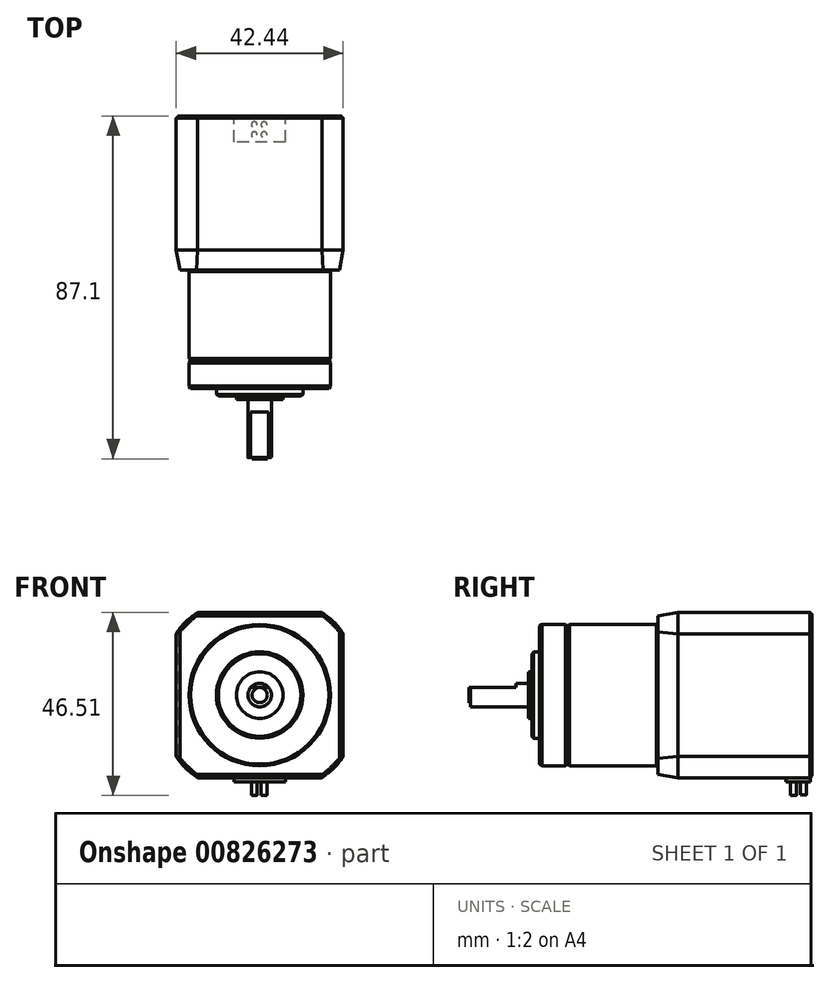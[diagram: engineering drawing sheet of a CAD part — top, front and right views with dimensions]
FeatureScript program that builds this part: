
annotation { "Feature Type Name" : "Feature", "Feature Type Description" : "" }
export const myFeature = defineFeature(function(context is Context, id is Id, definition is map)
    precondition{}
    {
        {
            var Q0;
            Q0=qCreatedBy(makeId("Front.planeOp"),FACE);
            var sketch = newSketch(context, id + "F0", { "sketchPlane" : qUnion([Q0])});
            skLineSegment(sketch, "E0", {"start": v(-21.22, -15.53) * mm, "end": v(-21.22, 15.53) * mm});
            skLineSegment(sketch, "E1", {"start": v(-6.73, -22.34) * mm, "end": v(6.27, -22.34) * mm});
            skFitSpline(sketch, "E2", {"points": [v(-21.22, 15.53) * mm, v(-15.77, 21) * mm], "startDerivative": vector(4.94, 6.8) * mm, "endDerivative": vector(6.38, 4.96) * mm});
            skFitSpline(sketch, "E3", {"points": [v(-20.22, 16.05) * mm, v(-16.08, 20.16) * mm], "startDerivative": vector(4, 4.56) * mm, "endDerivative": vector(4.18, 3.78) * mm});
            skLineSegment(sketch, "E4", {"start": v(-16.83, 20.16) * mm, "end": v(-16.08, 20.16) * mm});
            skLineSegment(sketch, "E5", {"start": v(-20.22, 16.82) * mm, "end": v(-20.22, 16.05) * mm});
            skCircle(sketch, "E6", {"center": v(-15.75, 15.5) * mm, "radius": 2.2 * mm});
            skCircle(sketch, "E7", {"center": v(-15.75, 15.5) * mm, "radius": 2.5 * mm});
            skLineSegment(sketch, "E8", {"start": v(-16.76, 15.5) * mm, "end": v(-16.76, 16.1) * mm});
            skLineSegment(sketch, "E9", {"start": v(-16.76, 16.1) * mm, "end": v(-16.35, 16.53) * mm});
            skLineSegment(sketch, "E10", {"start": v(-16.35, 16.53) * mm, "end": v(-15.75, 16.53) * mm});
            skLineSegment(sketch, "E11", {"start": v(-15.75, 15.5) * mm, "end": v(-15.75, 16.53) * mm});
            skLineSegment(sketch, "E12", {"start": v(-15.75, 15.5) * mm, "end": v(-16.76, 15.5) * mm});
            skLineSegment(sketch, "E13", {"start": v(-15.75, 15.5) * mm, "end": v(-15.78, 18.62) * mm, "construction": true});
            skLineSegment(sketch, "E14", {"start": v(-15.75, 15.5) * mm, "end": v(-15.73, 12.29) * mm, "construction": true});
            skLineSegment(sketch, "E15", {"start": v(-15.73, 12.29) * mm, "end": v(-15.75, 15.5) * mm, "construction": true});
            skLineSegment(sketch, "E16", {"start": v(-15.75, 15.5) * mm, "end": v(-12.33, 15.53) * mm, "construction": true});
            skLineSegment(sketch, "E17", {"start": v(-15.75, 15.5) * mm, "end": v(-18.75, 15.48) * mm, "construction": true});
            skLineSegment(sketch, "E18.MirrorCS", {"start": v(-15.17, 16.54) * mm, "end": v(-15.77, 16.53) * mm});
            skLineSegment(sketch, "E19.MirrorCS", {"start": v(-14.75, 16.1) * mm, "end": v(-15.17, 16.54) * mm});
            skLineSegment(sketch, "E20.MirrorCS", {"start": v(-14.75, 15.5) * mm, "end": v(-14.75, 16.1) * mm});
            skLineSegment(sketch, "E21.MirrorCS", {"start": v(-14.75, 15.5) * mm, "end": v(-14.75, 14.9) * mm});
            skLineSegment(sketch, "E22.MirrorCS", {"start": v(-14.75, 14.9) * mm, "end": v(-15.15, 14.47) * mm});
            skLineSegment(sketch, "E23.MirrorCS", {"start": v(-15.15, 14.47) * mm, "end": v(-15.75, 14.47) * mm});
            skLineSegment(sketch, "E24.MirrorCS", {"start": v(-16.34, 14.46) * mm, "end": v(-15.74, 14.47) * mm});
            skLineSegment(sketch, "E25.MirrorCS", {"start": v(-16.75, 14.9) * mm, "end": v(-16.34, 14.46) * mm});
            skLineSegment(sketch, "E26.MirrorCS", {"start": v(-16.76, 15.5) * mm, "end": v(-16.75, 14.9) * mm});
            skLineSegment(sketch, "E27", {"start": v(0, 0) * mm, "end": v(-21.22, 0) * mm, "construction": true});
            skLineSegment(sketch, "E28", {"start": v(0, 0) * mm, "end": v(0, 21) * mm, "construction": true});
            skCircle(sketch, "E29.MirrorC", {"center": v(15.75, 15.5) * mm, "radius": 2.2 * mm});
            skCircle(sketch, "E30.MirrorC", {"center": v(15.75, 15.5) * mm, "radius": 2.5 * mm});
            skLineSegment(sketch, "E31.MirrorCS", {"start": v(14.75, 15.5) * mm, "end": v(14.75, 14.9) * mm});
            skLineSegment(sketch, "E32.MirrorCS", {"start": v(14.75, 15.5) * mm, "end": v(14.75, 16.1) * mm});
            skLineSegment(sketch, "E33.MirrorCS", {"start": v(14.75, 16.1) * mm, "end": v(15.17, 16.54) * mm});
            skLineSegment(sketch, "E34.MirrorCS", {"start": v(15.17, 16.54) * mm, "end": v(15.77, 16.53) * mm});
            skLineSegment(sketch, "E35.MirrorCS", {"start": v(16.35, 16.53) * mm, "end": v(15.75, 16.53) * mm});
            skLineSegment(sketch, "E36.MirrorCS", {"start": v(16.76, 16.1) * mm, "end": v(16.35, 16.53) * mm});
            skLineSegment(sketch, "E37.MirrorCS", {"start": v(16.76, 15.5) * mm, "end": v(16.76, 16.1) * mm});
            skLineSegment(sketch, "E38.MirrorCS", {"start": v(16.76, 15.5) * mm, "end": v(16.75, 14.9) * mm});
            skLineSegment(sketch, "E39.MirrorCS", {"start": v(16.75, 14.9) * mm, "end": v(16.34, 14.46) * mm});
            skLineSegment(sketch, "E40.MirrorCS", {"start": v(16.34, 14.46) * mm, "end": v(15.74, 14.47) * mm});
            skLineSegment(sketch, "E41.MirrorCS", {"start": v(15.75, 15.5) * mm, "end": v(18.75, 15.48) * mm, "construction": true});
            skLineSegment(sketch, "E42.MirrorCS", {"start": v(15.75, 15.5) * mm, "end": v(12.33, 15.53) * mm, "construction": true});
            skLineSegment(sketch, "E43.MirrorCS", {"start": v(15.75, 15.5) * mm, "end": v(15.78, 18.62) * mm, "construction": true});
            skLineSegment(sketch, "E44.MirrorCS", {"start": v(15.75, 15.5) * mm, "end": v(15.73, 12.29) * mm, "construction": true});
            skFitSpline(sketch, "E45.MirrorCS", {"points": [v(21.22, 15.53) * mm, v(15.77, 21) * mm], "startDerivative": vector(-4.94, 6.8) * mm, "endDerivative": vector(-6.38, 4.96) * mm});
            skFitSpline(sketch, "E46.MirrorCS", {"points": [v(20.22, 16.05) * mm, v(16.08, 20.16) * mm], "startDerivative": vector(-4, 4.56) * mm, "endDerivative": vector(-4.18, 3.78) * mm});
            skLineSegment(sketch, "E47.MirrorCS", {"start": v(16.83, 20.16) * mm, "end": v(16.08, 20.16) * mm});
            skLineSegment(sketch, "E48", {"start": v(-15.77, 21) * mm, "end": v(0, 21) * mm});
            skLineSegment(sketch, "E49.MirrorCS", {"start": v(15.77, 21) * mm, "end": v(0, 21) * mm});
            skLineSegment(sketch, "E50.MirrorCS", {"start": v(20.22, 16.82) * mm, "end": v(20.22, 16.05) * mm});
            skLineSegment(sketch, "E51.MirrorCS", {"start": v(21.22, -15.53) * mm, "end": v(21.22, 15.53) * mm});
            skLineSegment(sketch, "E52.MirrorCS", {"start": v(-15.77, -21) * mm, "end": v(0, -21) * mm});
            skLineSegment(sketch, "E53.MirrorCS", {"start": v(-16.83, -20.16) * mm, "end": v(-16.08, -20.16) * mm});
            skFitSpline(sketch, "E54.MirrorCS", {"points": [v(-20.22, -16.05) * mm, v(-16.08, -20.16) * mm], "startDerivative": vector(4, -4.56) * mm, "endDerivative": vector(4.18, -3.78) * mm});
            skFitSpline(sketch, "E55.MirrorCS", {"points": [v(-21.22, -15.53) * mm, v(-15.77, -21) * mm], "startDerivative": vector(4.94, -6.8) * mm, "endDerivative": vector(6.38, -4.96) * mm});
            skLineSegment(sketch, "E56.MirrorCS", {"start": v(-20.22, -16.82) * mm, "end": v(-20.22, -16.05) * mm});
            skLineSegment(sketch, "E57.MirrorCS", {"start": v(-21.22, 15.53) * mm, "end": v(-21.22, -15.53) * mm});
            skCircle(sketch, "E58.MirrorC", {"center": v(-15.75, -15.5) * mm, "radius": 2.5 * mm});
            skCircle(sketch, "E59.MirrorC", {"center": v(-15.75, -15.5) * mm, "radius": 2.2 * mm});
            skLineSegment(sketch, "E60.MirrorCS", {"start": v(-16.75, -14.9) * mm, "end": v(-16.34, -14.46) * mm});
            skLineSegment(sketch, "E61.MirrorCS", {"start": v(-16.34, -14.46) * mm, "end": v(-15.74, -14.47) * mm});
            skLineSegment(sketch, "E62.MirrorCS", {"start": v(-15.15, -14.47) * mm, "end": v(-15.75, -14.47) * mm});
            skLineSegment(sketch, "E63.MirrorCS", {"start": v(-15.17, -16.54) * mm, "end": v(-15.77, -16.53) * mm});
            skLineSegment(sketch, "E64.MirrorCS", {"start": v(-14.75, -16.1) * mm, "end": v(-15.17, -16.54) * mm});
            skLineSegment(sketch, "E65.MirrorCS", {"start": v(-14.75, -15.5) * mm, "end": v(-14.75, -16.1) * mm});
            skLineSegment(sketch, "E66.MirrorCS", {"start": v(-14.75, -15.5) * mm, "end": v(-14.75, -14.9) * mm});
            skLineSegment(sketch, "E67.MirrorCS", {"start": v(-14.75, -14.9) * mm, "end": v(-15.15, -14.47) * mm});
            skLineSegment(sketch, "E68.MirrorCS", {"start": v(-16.76, -15.5) * mm, "end": v(-16.75, -14.9) * mm});
            skLineSegment(sketch, "E69.MirrorCS", {"start": v(-16.76, -16.1) * mm, "end": v(-16.35, -16.53) * mm});
            skLineSegment(sketch, "E70.MirrorCS", {"start": v(-16.76, -15.5) * mm, "end": v(-16.76, -16.1) * mm});
            skLineSegment(sketch, "E71.MirrorCS", {"start": v(-16.35, -16.53) * mm, "end": v(-15.75, -16.53) * mm});
            skLineSegment(sketch, "E72.MirrorCS", {"start": v(14.75, 14.9) * mm, "end": v(15.15, 14.47) * mm});
            skLineSegment(sketch, "E73.MirrorCS", {"start": v(15.15, 14.47) * mm, "end": v(15.75, 14.47) * mm});
            skLineSegment(sketch, "E74.MirrorCS", {"start": v(16.83, -20.16) * mm, "end": v(16.08, -20.16) * mm});
            skLineSegment(sketch, "E75.MirrorCS", {"start": v(15.77, -21) * mm, "end": v(0, -21) * mm});
            skFitSpline(sketch, "E76.MirrorCS", {"points": [v(21.22, -15.53) * mm, v(15.77, -21) * mm], "startDerivative": vector(-4.94, -6.8) * mm, "endDerivative": vector(-6.38, -4.96) * mm});
            skFitSpline(sketch, "E77.MirrorCS", {"points": [v(20.22, -16.05) * mm, v(16.08, -20.16) * mm], "startDerivative": vector(-4, -4.56) * mm, "endDerivative": vector(-4.18, -3.78) * mm});
            skLineSegment(sketch, "E78.MirrorCS", {"start": v(20.22, -16.82) * mm, "end": v(20.22, -16.05) * mm});
            skCircle(sketch, "E79.MirrorC", {"center": v(15.75, -15.5) * mm, "radius": 2.2 * mm});
            skCircle(sketch, "E80.MirrorC", {"center": v(15.75, -15.5) * mm, "radius": 2.5 * mm});
            skLineSegment(sketch, "E81.MirrorCS", {"start": v(16.75, -14.9) * mm, "end": v(16.34, -14.46) * mm});
            skLineSegment(sketch, "E82.MirrorCS", {"start": v(16.34, -14.46) * mm, "end": v(15.74, -14.47) * mm});
            skLineSegment(sketch, "E83.MirrorCS", {"start": v(15.15, -14.47) * mm, "end": v(15.75, -14.47) * mm});
            skLineSegment(sketch, "E84.MirrorCS", {"start": v(14.75, -14.9) * mm, "end": v(15.15, -14.47) * mm});
            skLineSegment(sketch, "E85.MirrorCS", {"start": v(14.75, -15.5) * mm, "end": v(14.75, -14.9) * mm});
            skLineSegment(sketch, "E86.MirrorCS", {"start": v(14.75, -15.5) * mm, "end": v(14.75, -16.1) * mm});
            skLineSegment(sketch, "E87.MirrorCS", {"start": v(14.75, -16.1) * mm, "end": v(15.17, -16.54) * mm});
            skLineSegment(sketch, "E88.MirrorCS", {"start": v(15.17, -16.54) * mm, "end": v(15.77, -16.53) * mm});
            skLineSegment(sketch, "E89.MirrorCS", {"start": v(16.35, -16.53) * mm, "end": v(15.75, -16.53) * mm});
            skLineSegment(sketch, "E90.MirrorCS", {"start": v(16.76, -16.1) * mm, "end": v(16.35, -16.53) * mm});
            skLineSegment(sketch, "E91.MirrorCS", {"start": v(16.76, -15.5) * mm, "end": v(16.76, -16.1) * mm});
            skLineSegment(sketch, "E92.MirrorCS", {"start": v(16.76, -15.5) * mm, "end": v(16.75, -14.9) * mm});
            skLineSegment(sketch, "E93", {"start": v(-16.08, 20.16) * mm, "end": v(0, 20.16) * mm});
            skFitSpline(sketch, "E94", {"points": [v(21.22, 15.53) * mm, v(15.77, 21) * mm], "startDerivative": vector(-4.94, 6.8) * mm, "endDerivative": vector(-6.38, 4.96) * mm});
            skLineSegment(sketch, "E95", {"start": v(16.08, 20.16) * mm, "end": v(16.08, 20.16) * mm});
            skLineSegment(sketch, "E96", {"start": v(16.08, 20.16) * mm, "end": v(0, 20.16) * mm});
            skLineSegment(sketch, "E97", {"start": v(16.08, -20.16) * mm, "end": v(0, -20.16) * mm});
            skFitSpline(sketch, "E98", {"points": [v(21.22, -15.53) * mm, v(15.77, -21) * mm], "startDerivative": vector(-4.94, -6.8) * mm, "endDerivative": vector(-6.38, -4.96) * mm});
            skFitSpline(sketch, "E99", {"points": [v(21.22, -15.53) * mm, v(15.77, -21) * mm], "startDerivative": vector(-4.94, -6.8) * mm, "endDerivative": vector(-6.38, -4.96) * mm});
            skLineSegment(sketch, "E100", {"start": v(-16.08, -20.16) * mm, "end": v(0, -20.16) * mm});
            skLineSegment(sketch, "E101", {"start": v(20.22, 16.05) * mm, "end": v(20.22, -16.05) * mm});
            skLineSegment(sketch, "E102", {"start": v(-20.22, 16.05) * mm, "end": v(-20.22, -16.05) * mm});
            skSolve(sketch);
        }
        {
            var Q0;
            Q0=qCreatedBy(makeId("Right.planeOp"),FACE);
            var sketch = newSketch(context, id + "F1", { "sketchPlane" : qUnion([Q0])});
            skLineSegment(sketch, "E103", {"start": v(9.44, 20.64) * mm, "end": v(9.44, -20.64) * mm});
            skLineSegment(sketch, "E104", {"start": v(43.44, 20.64) * mm, "end": v(43.44, -20.64) * mm});
            skLineSegment(sketch, "E105", {"start": v(9.44, -20.64) * mm, "end": v(43.44, -20.64) * mm});
            skLineSegment(sketch, "E106", {"start": v(9.44, 20.64) * mm, "end": v(43.44, 20.64) * mm});
            skLineSegment(sketch, "E107", {"start": v(43.44, 0) * mm, "end": v(54.68, 0) * mm});
            skLineSegment(sketch, "E108", {"start": v(-43.56, 0) * mm, "end": v(43.44, 0) * mm});
            skLineSegment(sketch, "E109", {"start": v(9.44, 20.64) * mm, "end": v(-0.08, 20.64) * mm});
            skLineSegment(sketch, "E110", {"start": v(-0.08, 20.64) * mm, "end": v(-0.08, 1.4) * mm, "construction": true});
            skLineSegment(sketch, "E111", {"start": v(-43.25, -3.17) * mm, "end": v(-29.97, -3.17) * mm});
            skLineSegment(sketch, "E112", {"start": v(-29.97, -3.17) * mm, "end": v(-29.97, 0) * mm});
            skLineSegment(sketch, "E113", {"start": v(-29.97, 2.99) * mm, "end": v(-31.68, 2.99) * mm});
            skLineSegment(sketch, "E114", {"start": v(-31.68, 2.99) * mm, "end": v(-31.68, 1.93) * mm});
            skLineSegment(sketch, "E115", {"start": v(-31.68, 1.93) * mm, "end": v(-43.58, 1.93) * mm});
            skLineSegment(sketch, "E116", {"start": v(-43.56, 1.93) * mm, "end": v(-43.58, 1.93) * mm});
            skLineSegment(sketch, "E117", {"start": v(-43.56, 0) * mm, "end": v(-43.56, 1.93) * mm});
            skLineSegment(sketch, "E118", {"start": v(-43.56, 0) * mm, "end": v(-43.56, -2.8) * mm});
            skLineSegment(sketch, "E119", {"start": v(-43.56, -2.8) * mm, "end": v(-43.25, -3.17) * mm});
            skLineSegment(sketch, "E120", {"start": v(-29.97, 0) * mm, "end": v(-29.97, 2.99) * mm});
            skLineSegment(sketch, "E121", {"start": v(-29.97, 2.99) * mm, "end": v(-28.48, 2.99) * mm});
            skLineSegment(sketch, "E122", {"start": v(-28.48, 2.99) * mm, "end": v(-28.48, 0) * mm});
            skLineSegment(sketch, "E123", {"start": v(-28.48, 2.99) * mm, "end": v(-28.48, 5.94) * mm});
            skLineSegment(sketch, "E124", {"start": v(-28.48, 5.94) * mm, "end": v(-27.62, 5.94) * mm});
            skLineSegment(sketch, "E125", {"start": v(-27.62, 5.94) * mm, "end": v(-27.62, 0) * mm});
            skLineSegment(sketch, "E126", {"start": v(-27.62, 5.94) * mm, "end": v(-27.62, 10.48) * mm});
            skLineSegment(sketch, "E127", {"start": v(-27.62, 10.48) * mm, "end": v(-27.18, 11) * mm});
            skLineSegment(sketch, "E128", {"start": v(-27.18, 11) * mm, "end": v(-25.71, 11) * mm});
            skLineSegment(sketch, "E129", {"start": v(-27.18, 11) * mm, "end": v(-27.18, 0) * mm});
            skLineSegment(sketch, "E130", {"start": v(-27.18, 0) * mm, "end": v(-27.62, 0) * mm});
            skLineSegment(sketch, "E131", {"start": v(-27.18, 0) * mm, "end": v(-25.71, 0) * mm});
            skLineSegment(sketch, "E132", {"start": v(-25.71, 0) * mm, "end": v(-25.71, 17.55) * mm});
            skLineSegment(sketch, "E133", {"start": v(-25.71, 17.55) * mm, "end": v(-25.09, 17.95) * mm});
            skLineSegment(sketch, "E134", {"start": v(-25.09, 17.95) * mm, "end": v(-25.09, 0) * mm});
            skLineSegment(sketch, "E135", {"start": v(-25.09, 0) * mm, "end": v(-25.71, 0) * mm});
            skLineSegment(sketch, "E136", {"start": v(-25.09, 17.95) * mm, "end": v(-19.16, 17.95) * mm});
            skLineSegment(sketch, "E137", {"start": v(-19.16, 17.95) * mm, "end": v(-19.16, 0) * mm});
            skLineSegment(sketch, "E138", {"start": v(-19.16, 0) * mm, "end": v(-25.09, 0) * mm});
            skLineSegment(sketch, "E139", {"start": v(-19.16, 17.95) * mm, "end": v(-18.54, 17.54) * mm});
            skLineSegment(sketch, "E140", {"start": v(-18.54, 17.54) * mm, "end": v(-18.54, 0) * mm});
            skLineSegment(sketch, "E141", {"start": v(-18.54, 0) * mm, "end": v(-19.16, 0) * mm});
            skLineSegment(sketch, "E142", {"start": v(-18.54, 17.54) * mm, "end": v(-18.12, 17.95) * mm});
            skLineSegment(sketch, "E143", {"start": v(-18.12, 17.95) * mm, "end": v(-18.12, 0) * mm});
            skLineSegment(sketch, "E144", {"start": v(-18.12, 17.95) * mm, "end": v(4.03, 17.95) * mm});
            skLineSegment(sketch, "E145", {"start": v(4.03, 17.95) * mm, "end": v(4.03, 0) * mm});
            skLineSegment(sketch, "E146", {"start": v(4.43, 0) * mm, "end": v(4.43, 19.49) * mm});
            skLineSegment(sketch, "E147", {"start": v(4.03, 17.76) * mm, "end": v(4.43, 17.76) * mm});
            skLineSegment(sketch, "E148", {"start": v(4.93, 16.51) * mm, "end": v(4.93, 20.1) * mm});
            skLineSegment(sketch, "E149", {"start": v(4.93, 20.1) * mm, "end": v(8.94, 20.1) * mm});
            skLineSegment(sketch, "E150", {"start": v(8.94, 20.1) * mm, "end": v(8.94, 16.7) * mm});
            skLineSegment(sketch, "E151", {"start": v(8.94, 16.7) * mm, "end": v(4.93, 16.7) * mm});
            skLineSegment(sketch, "E152", {"start": v(8.94, 20.1) * mm, "end": v(9.44, 19.55) * mm});
            skLineSegment(sketch, "E153", {"start": v(4.43, 19.49) * mm, "end": v(4.93, 20.1) * mm});
            skLineSegment(sketch, "E154", {"start": v(4.93, 16.51) * mm, "end": v(8.94, 16.51) * mm});
            skLineSegment(sketch, "E155", {"start": v(8.94, 16.51) * mm, "end": v(9.44, 16.22) * mm});
            skLineSegment(sketch, "E156", {"start": v(4.93, 16.51) * mm, "end": v(4.43, 16.14) * mm});
            skLineSegment(sketch, "E157", {"start": v(8.94, 16.7) * mm, "end": v(8.94, 16.51) * mm});
            skLineSegment(sketch, "E158", {"start": v(9.44, 20.64) * mm, "end": v(9.83, 20.99) * mm});
            skLineSegment(sketch, "E159", {"start": v(9.83, 20.99) * mm, "end": v(43.06, 20.99) * mm});
            skLineSegment(sketch, "E160", {"start": v(43.06, 20.99) * mm, "end": v(43.06, 0) * mm});
            skLineSegment(sketch, "E161", {"start": v(43.06, 20.99) * mm, "end": v(43.44, 20.64) * mm});
            skLineSegment(sketch, "E162", {"start": v(9.83, 20.99) * mm, "end": v(9.83, 0) * mm});
            skLineSegment(sketch, "E163", {"start": v(9.83, 15.23) * mm, "end": v(17.52, 15.23) * mm});
            skLineSegment(sketch, "E164", {"start": v(9.83, 15.23) * mm, "end": v(9.44, 14.97) * mm});
            skLineSegment(sketch, "E165", {"start": v(17.52, 15.23) * mm, "end": v(35.49, 15.23) * mm, "construction": true});
            skLineSegment(sketch, "E166", {"start": v(43.06, 15.23) * mm, "end": v(35.49, 15.23) * mm});
            skLineSegment(sketch, "E167", {"start": v(17.57, 12.9) * mm, "end": v(35.52, 12.9) * mm});
            skLineSegment(sketch, "E168", {"start": v(35.52, 20.99) * mm, "end": v(35.52, 0) * mm});
            skLineSegment(sketch, "E169", {"start": v(35.52, 0) * mm, "end": v(34.87, 0) * mm});
            skLineSegment(sketch, "E170", {"start": v(34.87, 0) * mm, "end": v(34.87, 20.99) * mm});
            skLineSegment(sketch, "E171", {"start": v(34.87, 0) * mm, "end": v(33.38, 0) * mm});
            skLineSegment(sketch, "E172", {"start": v(33.38, 0) * mm, "end": v(33.38, 20.99) * mm});
            skLineSegment(sketch, "E173", {"start": v(33.38, 0) * mm, "end": v(31.9, 0) * mm});
            skLineSegment(sketch, "E174", {"start": v(31.9, 0) * mm, "end": v(31.9, 20.99) * mm});
            skLineSegment(sketch, "E175", {"start": v(31.9, 0) * mm, "end": v(30.21, 0) * mm});
            skLineSegment(sketch, "E176", {"start": v(30.21, 0) * mm, "end": v(30.21, 20.99) * mm});
            skLineSegment(sketch, "E177", {"start": v(30.21, 0) * mm, "end": v(28.76, 0) * mm});
            skLineSegment(sketch, "E178", {"start": v(28.76, 0) * mm, "end": v(28.76, 20.99) * mm});
            skLineSegment(sketch, "E179", {"start": v(28.76, 20.99) * mm, "end": v(27.27, 20.99) * mm});
            skLineSegment(sketch, "E180", {"start": v(27.27, 20.99) * mm, "end": v(27.27, 0) * mm});
            skLineSegment(sketch, "E181", {"start": v(27.27, 0) * mm, "end": v(28.76, 0) * mm});
            skLineSegment(sketch, "E182", {"start": v(27.27, 0) * mm, "end": v(25.81, 0) * mm});
            skLineSegment(sketch, "E183", {"start": v(25.81, 0) * mm, "end": v(25.81, 20.99) * mm});
            skLineSegment(sketch, "E184", {"start": v(25.81, 20.99) * mm, "end": v(24.32, 20.99) * mm});
            skLineSegment(sketch, "E185", {"start": v(24.32, 20.99) * mm, "end": v(24.32, 0) * mm});
            skLineSegment(sketch, "E186", {"start": v(24.32, 0) * mm, "end": v(25.81, 0) * mm});
            skLineSegment(sketch, "E187", {"start": v(22.86, 20.99) * mm, "end": v(22.86, 0) * mm});
            skLineSegment(sketch, "E188", {"start": v(22.86, 0) * mm, "end": v(21.36, 0) * mm});
            skLineSegment(sketch, "E189", {"start": v(21.36, 0) * mm, "end": v(21.36, 20.99) * mm});
            skLineSegment(sketch, "E190", {"start": v(21.36, 20.99) * mm, "end": v(19.9, 20.99) * mm});
            skLineSegment(sketch, "E191", {"start": v(19.9, 20.99) * mm, "end": v(19.9, 0) * mm});
            skLineSegment(sketch, "E192", {"start": v(19.9, 0) * mm, "end": v(21.36, 0) * mm});
            skLineSegment(sketch, "E193", {"start": v(18.21, 20.99) * mm, "end": v(18.21, 0) * mm});
            skLineSegment(sketch, "E194", {"start": v(18.21, 0) * mm, "end": v(19.9, 0) * mm});
            skLineSegment(sketch, "E195", {"start": v(17.52, 20.99) * mm, "end": v(17.57, 0) * mm});
            skLineSegment(sketch, "E196", {"start": v(17.57, 0) * mm, "end": v(18.21, 0) * mm});
            skLineSegment(sketch, "E197", {"start": v(9.44, 19.55) * mm, "end": v(4.43, 19.55) * mm, "construction": true});
            skLineSegment(sketch, "E198", {"start": v(-31.68, 2.99) * mm, "end": v(-43.58, 2.99) * mm});
            skLineSegment(sketch, "E199", {"start": v(-43.58, 2.99) * mm, "end": v(-43.58, 1.93) * mm});
            skLineSegment(sketch, "E200", {"start": v(-43.25, -3.17) * mm, "end": v(-43.25, 2.99) * mm});
            skLineSegment(sketch, "E201", {"start": v(-43.25, 2.99) * mm, "end": v(-43.58, 2.6) * mm});
            skSolve(sketch);
        }
        {
            var Q0;
            {var subQ0=sQuery(id+"F1.wireOp",EDGE,"E120");Q0=makeQuery(id+"F1.imprint","IMPRINT",FACE,{"disambiguationData":[TD([[makeQuery(id+"F1.imprint","IMPRINT",EDGE,{"derivedFrom":subQ0}),-1.0]])]});}
            var Q1;
            {var subQ0=sQuery(id+"F1.wireOp",EDGE,"E122");Q1=makeQuery(id+"F1.imprint","IMPRINT",FACE,{"disambiguationData":[TD([[makeQuery(id+"F1.imprint","IMPRINT",EDGE,{"derivedFrom":subQ0}),1.0]])]});}
            var Q2;
            Q2=makeQuery(id+"F1.imprint","IMPRINT",FACE,{"disambiguationData":[TD([[makeQuery(id+"F1.imprint","IMPRINT",EDGE,{"derivedFrom":sQuery(id+"F1.wireOp",EDGE,"E125")}),1.0]])]});
            var Q3;
            Q3=makeQuery(id+"F1.imprint","IMPRINT",FACE,{"disambiguationData":[TD([[makeQuery(id+"F1.imprint","IMPRINT",EDGE,{"derivedFrom":sQuery(id+"F1.wireOp",EDGE,"E132")}),-1.0]])]});
            var Q4;
            Q4=makeQuery(id+"F1.imprint","IMPRINT",FACE,{"disambiguationData":[TD([[makeQuery(id+"F1.imprint","IMPRINT",EDGE,{"derivedFrom":sQuery(id+"F1.wireOp",EDGE,"E134")}),1.0]])]});
            var Q5;
            Q5=makeQuery(id+"F1.imprint","IMPRINT",FACE,{"disambiguationData":[TD([[makeQuery(id+"F1.imprint","IMPRINT",EDGE,{"derivedFrom":sQuery(id+"F1.wireOp",EDGE,"E137")}),1.0]])]});
            var Q6;
            {var subQ0=sQuery(id+"F1.wireOp",EDGE,"E140");Q6=makeQuery(id+"F1.imprint","IMPRINT",FACE,{"disambiguationData":[TD([[makeQuery(id+"F1.imprint","IMPRINT",EDGE,{"derivedFrom":subQ0}),1.0]])]});}
            var Q7;
            {var subQ1=sQuery(id+"F1.wireOp",EDGE,"E143");Q7=makeQuery(id+"F1.imprint","IMPRINT",FACE,{"disambiguationData":[TD([[makeQuery(id+"F1.imprint","IMPRINT",EDGE,{"derivedFrom":subQ1}),1.0]])]});}
            var Q8;
            {var subQ0=sQuery(id+"F1.wireOp",EDGE,"E147");Q8=makeQuery(id+"F1.imprint","IMPRINT",FACE,{"disambiguationData":[TD([[makeQuery(id+"F1.imprint","IMPRINT",EDGE,{"derivedFrom":subQ0}),-1.0]])]});}
            var Q9;
            {var subQ0=sQuery(id+"F1.wireOp",EDGE,"E128");Q9=makeQuery(id+"F1.imprint","IMPRINT",FACE,{"disambiguationData":[TD([[makeQuery(id+"F1.imprint","IMPRINT",EDGE,{"derivedFrom":subQ0}),-1.0]])]});}
            var Q10;
            {var subQ0=sQuery(id+"F1.wireOp",EDGE,"E117");Q10=makeQuery(id+"F1.imprint","IMPRINT",FACE,{"disambiguationData":[TD([[makeQuery(id+"F1.imprint","IMPRINT",EDGE,{"derivedFrom":subQ0}),-1.0]])]});}
            var Q11;
            {var subQ1=sQuery(id+"F1.wireOp",EDGE,"E116");Q11=makeQuery(id+"F1.imprint","IMPRINT",FACE,{"disambiguationData":[TD([[makeQuery(id+"F1.imprint","IMPRINT",EDGE,{"derivedFrom":subQ1}),-1.0]])]});}
            var Q12;
            {var subQ0=sQuery(id+"F1.wireOp",EDGE,"E114");Q12=makeQuery(id+"F1.imprint","IMPRINT",FACE,{"disambiguationData":[TD([[makeQuery(id+"F1.imprint","IMPRINT",EDGE,{"derivedFrom":subQ0}),-1.0]])]});}
            var Q13;
            Q13=makeQuery(id+"F1.imprint","IMPRINT",FACE,{"disambiguationData":[TD([[makeQuery(id+"F1.imprint","IMPRINT",EDGE,{"derivedFrom":sQuery(id+"F1.wireOp",EDGE,"E113")}),1.0]])]});
            var Q14;
            Q14=sQuery(id+"F1.wireOp",EDGE,"E108");
            revolve(context, id + "F2", {"surfaceOperationType" : NewSurfaceOperationType.NEW, "entities" : qUnion([Q0, Q1, Q2, Q3, Q4, Q5, Q6, Q7, Q8, Q9, Q10, Q11, Q12, Q13]), "axis" : qUnion([Q14]), "revolveType" : RevolveType.FULL});
        }
        {
            var Q0;
            Q0=qCreatedBy(makeId("Right.planeOp"),FACE);
            var sketch = newSketch(context, id + "F3", { "sketchPlane" : qUnion([Q0])});
            skLineSegment(sketch, "E202", {"start": v(36.96, -20.95) * mm, "end": v(36.96, -22.1) * mm});
            skLineSegment(sketch, "E203", {"start": v(36.96, -22.1) * mm, "end": v(43.1, -22.1) * mm});
            skLineSegment(sketch, "E204", {"start": v(43.1, -22.1) * mm, "end": v(43.1, -20.95) * mm});
            skLineSegment(sketch, "E205", {"start": v(36.96, -20.95) * mm, "end": v(43.1, -20.95) * mm});
            skLineSegment(sketch, "E206", {"start": v(38.05, -22.1) * mm, "end": v(38.05, -25.5) * mm});
            skLineSegment(sketch, "E207", {"start": v(39.54, -22.1) * mm, "end": v(39.54, -25.5) * mm});
            skLineSegment(sketch, "E208", {"start": v(40.6, -22.1) * mm, "end": v(40.6, -25.4) * mm});
            skLineSegment(sketch, "E209", {"start": v(42.1, -22.1) * mm, "end": v(42.1, -25.4) * mm});
            skLineSegment(sketch, "E210", {"start": v(42.1, -25.4) * mm, "end": v(40.6, -25.4) * mm});
            skLineSegment(sketch, "E211", {"start": v(39.54, -25.5) * mm, "end": v(38.05, -25.5) * mm});
            skLineSegment(sketch, "E212", {"start": v(12.2, -23.58) * mm, "end": v(30.24, -23.58) * mm});
            skLineSegment(sketch, "E213", {"start": v(30.24, -23.58) * mm, "end": v(30.24, -25.3) * mm});
            skLineSegment(sketch, "E214", {"start": v(30.24, -25.3) * mm, "end": v(12.2, -25.3) * mm});
            skLineSegment(sketch, "E215", {"start": v(12.2, -25.3) * mm, "end": v(12.2, -23.58) * mm});
            skLineSegment(sketch, "E216", {"start": v(12.2, -24.91) * mm, "end": v(11.03, -24.91) * mm});
            skLineSegment(sketch, "E217", {"start": v(11.03, -24.91) * mm, "end": v(11.03, -24.03) * mm});
            skLineSegment(sketch, "E218", {"start": v(11.03, -24.03) * mm, "end": v(12.2, -24.03) * mm});
            skFitSpline(sketch, "E219", {"points": [v(35.92, -28.25) * mm, v(39.54, -25.5) * mm], "startDerivative": vector(5.88, -0.8) * mm, "endDerivative": vector(-0.22, 4.78) * mm});
            skLineSegment(sketch, "E220", {"start": v(35.92, -28.25) * mm, "end": v(30.24, -25.3) * mm});
            skFitSpline(sketch, "E221", {"points": [v(36, -26.63) * mm, v(38.05, -25.5) * mm], "startDerivative": vector(3.7, -1.62) * mm, "endDerivative": vector(-0.07, 2) * mm});
            skLineSegment(sketch, "E222", {"start": v(30.24, -23.58) * mm, "end": v(36, -26.63) * mm});
            skFitSpline(sketch, "E223", {"points": [v(37.95, -27.91) * mm, v(42.1, -25.4) * mm], "startDerivative": vector(6.7, -3.77) * mm, "endDerivative": vector(-0.84, 3.32) * mm});
            skFitSpline(sketch, "E224", {"points": [v(39.29, -26.63) * mm, v(40.6, -25.4) * mm], "startDerivative": vector(2.54, 0.49) * mm, "endDerivative": vector(0.07, 1.27) * mm});
            skLineSegment(sketch, "E225", {"start": v(30.24, -23.58) * mm, "end": v(30.72, -23.58) * mm});
            skLineSegment(sketch, "E226", {"start": v(30.72, -23.58) * mm, "end": v(37.74, -26.3) * mm});
            skLineSegment(sketch, "E227", {"start": v(38.05, -22.1) * mm, "end": v(39.54, -22.1) * mm});
            skLineSegment(sketch, "E228", {"start": v(40.6, -22.1) * mm, "end": v(42.1, -22.1) * mm});
            skLineSegment(sketch, "E229", {"start": v(38.8, -22.1) * mm, "end": v(38.8, -25.5) * mm});
            skLineSegment(sketch, "E230", {"start": v(41.35, -22.1) * mm, "end": v(41.35, -25.4) * mm});
            skLineSegment(sketch, "E231", {"start": v(35.92, -28.25) * mm, "end": v(36, -26.63) * mm});
            skLineSegment(sketch, "E232", {"start": v(30.24, -24.44) * mm, "end": v(35.96, -27.44) * mm});
            skLineSegment(sketch, "E233", {"start": v(12.2, -24.44) * mm, "end": v(30.24, -24.44) * mm});
            skLineSegment(sketch, "E234", {"start": v(12.2, -24.44) * mm, "end": v(11.03, -24.44) * mm});
            skFitSpline(sketch, "E235", {"points": [v(35.96, -27.44) * mm, v(38.8, -25.5) * mm], "startDerivative": vector(4.56, -1.56) * mm, "endDerivative": vector(-0.13, 2.93) * mm});
            skSolve(sketch);
        }
        {
            var Q0;
            {var subQ8=sQuery(id+"F3.wireOp",EDGE,"E202");Q0=makeQuery(id+"F3.imprint","IMPRINT",FACE,{"disambiguationData":[TD([[makeQuery(id+"F3.imprint","IMPRINT",EDGE,{"derivedFrom":subQ8}),1.0]])]});}
            extrude(context, id + "F4", {"entities" : qUnion([Q0]), "operationType" : NewBodyOperationType.ADD, "endBound" : BoundingType.SYMMETRIC, "depth" : 13 * mm, "offsetDistance" : 25 * mm});
        }
        {
            var Q0;
            {var subQ0=sQuery(id+"F3.wireOp",EDGE,"E206");Q0=makeQuery(id+"F3.imprint","IMPRINT",FACE,{"disambiguationData":[TD([[makeQuery(id+"F3.imprint","IMPRINT",EDGE,{"derivedFrom":subQ0}),1.0]])]});}
            var Q1;
            Q1=sQuery(id+"F3.wireOp",EDGE,"E229");
            revolve(context, id + "F5", {"surfaceOperationType" : NewSurfaceOperationType.NEW, "entities" : qUnion([Q0]), "axis" : qUnion([Q1]), "revolveType" : RevolveType.FULL});
        }
        {
            var Q0;
            {var subQ0=sQuery(id+"F3.wireOp",EDGE,"E208");Q0=makeQuery(id+"F3.imprint","IMPRINT",FACE,{"disambiguationData":[TD([[makeQuery(id+"F3.imprint","IMPRINT",EDGE,{"derivedFrom":subQ0}),1.0]])]});}
            var Q1;
            Q1=sQuery(id+"F3.wireOp",EDGE,"E230");
            revolve(context, id + "F6", {"surfaceOperationType" : NewSurfaceOperationType.NEW, "entities" : qUnion([Q0]), "axis" : qUnion([Q1]), "revolveType" : RevolveType.FULL});
        }
        {
            var Q0;
            Q0=makeQuery(id+"F5.opRevolve","SWEPT_BODY",BODY,{"disambiguationData":[OSD([sQuery(id+"F3.wireOp",EDGE,"E206"),sQuery(id+"F3.wireOp",EDGE,"E211"),sQuery(id+"F3.wireOp",EDGE,"E227"),sQuery(id+"F3.wireOp",EDGE,"E229")])]});
            var Q1;
            Q1=makeQuery(id+"F6.opRevolve","SWEPT_BODY",BODY,{"disambiguationData":[OSD([sQuery(id+"F3.wireOp",EDGE,"E208"),sQuery(id+"F3.wireOp",EDGE,"E210"),sQuery(id+"F3.wireOp",EDGE,"E228"),sQuery(id+"F3.wireOp",EDGE,"E230")])]});
            transform(context, id + "F7", {"entities" : qUnion([Q0, Q1]), "transformType" : TransformType.TRANSLATION_3D, "dx" : 1.1 * mm, "dy" : 0 * mm, "dz" : 0 * mm, "makeCopy" : false});
        }
        {
            var Q0;
            Q0=makeQuery(id+"F5.opRevolve","SWEPT_BODY",BODY,{"disambiguationData":[OSD([sQuery(id+"F3.wireOp",EDGE,"E206"),sQuery(id+"F3.wireOp",EDGE,"E211"),sQuery(id+"F3.wireOp",EDGE,"E227"),sQuery(id+"F3.wireOp",EDGE,"E229")])]});
            var Q1;
            Q1=makeQuery(id+"F6.opRevolve","SWEPT_BODY",BODY,{"disambiguationData":[OSD([sQuery(id+"F3.wireOp",EDGE,"E208"),sQuery(id+"F3.wireOp",EDGE,"E210"),sQuery(id+"F3.wireOp",EDGE,"E228"),sQuery(id+"F3.wireOp",EDGE,"E230")])]});
            transform(context, id + "F8", {"entities" : qUnion([Q0, Q1]), "transformType" : TransformType.TRANSLATION_3D, "dx" : -2.48 * mm, "dy" : 0 * mm, "dz" : 0 * mm, "makeCopy" : true});
        }
        {
            var Q0;
            {var subQ0=sQuery(id+"F1.wireOp",EDGE,"E114");Q0=makeQuery(id+"F1.imprint","IMPRINT",FACE,{"disambiguationData":[TD([[makeQuery(id+"F1.imprint","IMPRINT",EDGE,{"derivedFrom":subQ0}),-1.0]])]});}
            var Q1;
            {var subQ3=sQuery(id+"F1.wireOp",EDGE,"E201");Q1=makeQuery(id+"F1.imprint","IMPRINT",FACE,{"disambiguationData":[TD([[makeQuery(id+"F1.imprint","IMPRINT",EDGE,{"derivedFrom":subQ3}),-1.0]])]});}
            extrude(context, id + "F9", {"entities" : qUnion([Q0, Q1]), "operationType" : NewBodyOperationType.REMOVE, "endBound" : BoundingType.SYMMETRIC, "oppositeDirection" : true, "depth" : 25 * mm, "offsetDistance" : 25 * mm});
        }
        {
            var Q0;
            Q0=qCreatedBy(makeId("Front.planeOp"),FACE);
            cPlane(context, id + "F10", {"entities" : qUnion([Q0]), "cplaneType" : CPlaneType.OFFSET, "offset" : 4.43 * mm, "oppositeDirection" : true, "width" : 150 * mm, "height" : 150 * mm});
        }
        {
            var Q0;
            Q0=qCreatedBy(id+"F10.planeOp",FACE);
            var sketch = newSketch(context, id + "F11", { "sketchPlane" : qUnion([Q0])});
            skFitSpline(sketch, "E236.0", {"points": [v(20.22, -16.05) * mm, v(18.88, -17.56) * mm, v(17.47, -18.9) * mm, v(16.08, -20.16) * mm]});
            skLineSegment(sketch, "E237.0", {"start": v(16.08, -20.16) * mm, "end": v(0, -20.16) * mm});
            skLineSegment(sketch, "E238.0", {"start": v(-16.08, -20.16) * mm, "end": v(0, -20.16) * mm});
            skFitSpline(sketch, "E239.0", {"points": [v(-20.22, -16.05) * mm, v(-18.88, -17.56) * mm, v(-17.47, -18.9) * mm, v(-16.08, -20.16) * mm]});
            skFitSpline(sketch, "E240.0", {"points": [v(-20.22, 16.05) * mm, v(-18.88, 17.56) * mm, v(-17.47, 18.9) * mm, v(-16.08, 20.16) * mm]});
            skLineSegment(sketch, "E241.0", {"start": v(-16.08, 20.16) * mm, "end": v(0, 20.16) * mm});
            skLineSegment(sketch, "E242.0", {"start": v(16.08, 20.16) * mm, "end": v(0, 20.16) * mm});
            skFitSpline(sketch, "E243.0", {"points": [v(20.22, 16.05) * mm, v(18.88, 17.56) * mm, v(17.47, 18.9) * mm, v(16.08, 20.16) * mm]});
            skLineSegment(sketch, "E244", {"start": v(20.22, 16.05) * mm, "end": v(20.22, -16.05) * mm});
            skLineSegment(sketch, "E245", {"start": v(-20.22, 16.05) * mm, "end": v(-20.22, -16.05) * mm});
            skSolve(sketch);
        }
        {
            var Q0;
            Q0=qCreatedBy(makeId("Front.planeOp"),FACE);
            cPlane(context, id + "F12", {"entities" : qUnion([Q0]), "cplaneType" : CPlaneType.OFFSET, "offset" : 9.44 * mm, "oppositeDirection" : true, "width" : 150 * mm, "height" : 150 * mm});
        }
        {
            var Q0;
            Q0=qCreatedBy(id+"F12.planeOp",FACE);
            var sketch = newSketch(context, id + "F13", { "sketchPlane" : qUnion([Q0])});
            skFitSpline(sketch, "E246.0", {"points": [v(21.22, 15.53) * mm, v(19.57, 17.8) * mm, v(17.9, 19.35) * mm, v(15.77, 21) * mm]});
            skFitSpline(sketch, "E247.0", {"points": [v(21.22, 15.53) * mm, v(19.57, 17.8) * mm, v(17.9, 19.35) * mm, v(15.77, 21) * mm]});
            skLineSegment(sketch, "E248.0", {"start": v(15.77, 21) * mm, "end": v(0, 21) * mm});
            skLineSegment(sketch, "E249.0", {"start": v(-15.77, 21) * mm, "end": v(0, 21) * mm});
            skFitSpline(sketch, "E250.0", {"points": [v(-21.22, 15.53) * mm, v(-19.57, 17.8) * mm, v(-17.9, 19.35) * mm, v(-15.77, 21) * mm]});
            skLineSegment(sketch, "E251.0", {"start": v(-21.22, 15.53) * mm, "end": v(-21.22, -15.53) * mm});
            skFitSpline(sketch, "E252.0", {"points": [v(-21.22, -15.53) * mm, v(-19.57, -17.8) * mm, v(-17.9, -19.35) * mm, v(-15.77, -21) * mm]});
            skFitSpline(sketch, "E253.0", {"points": [v(-21.22, -15.53) * mm, v(-19.57, -17.8) * mm, v(-17.9, -19.35) * mm, v(-15.77, -21) * mm]});
            skFitSpline(sketch, "E254.0", {"points": [v(-21.22, -15.53) * mm, v(-19.57, -17.8) * mm, v(-17.9, -19.35) * mm, v(-15.77, -21) * mm]});
            skLineSegment(sketch, "E255.0", {"start": v(-15.77, -21) * mm, "end": v(0, -21) * mm});
            skLineSegment(sketch, "E256.0", {"start": v(15.77, -21) * mm, "end": v(0, -21) * mm});
            skFitSpline(sketch, "E257.0", {"points": [v(21.22, -15.53) * mm, v(19.57, -17.8) * mm, v(17.9, -19.35) * mm, v(15.77, -21) * mm]});
            skFitSpline(sketch, "E258.0", {"points": [v(21.22, -15.53) * mm, v(19.57, -17.8) * mm, v(17.9, -19.35) * mm, v(15.77, -21) * mm]});
            skFitSpline(sketch, "E259.0", {"points": [v(21.22, -15.53) * mm, v(19.57, -17.8) * mm, v(17.9, -19.35) * mm, v(15.77, -21) * mm]});
            skLineSegment(sketch, "E260.0", {"start": v(21.22, -15.53) * mm, "end": v(21.22, 15.53) * mm});
            skSolve(sketch);
        }
        {
            var Q0;
            Q0=sQuery(id+"F13.wireOp",VERTEX,"E249.0.start");
            var Q1;
            Q1=sQuery(id+"F11.wireOp",VERTEX,"E240.0.end");
            var Q2;
            Q2=sQuery(id+"F13.wireOp",VERTEX,"E254.0.end");
            cPlane(context, id + "F14", {"entities" : qUnion([Q0, Q1, Q2]), "cplaneType" : CPlaneType.THREE_POINT, "offset" : 25 * mm, "width" : 150 * mm, "height" : 150 * mm});
        }
        {
            var Q0;
            Q0=qCreatedBy(id+"F14.planeOp",FACE);
            var sketch = newSketch(context, id + "F15", { "sketchPlane" : qUnion([Q0])});
            skPoint(sketch, "E261.0", {"position": v(-3.43, 20.16) * mm});
            skPoint(sketch, "E262.0", {"position": v(-8.45, 21) * mm});
            skLineSegment(sketch, "E263", {"start": v(-8.45, 21) * mm, "end": v(-3.43, 20.16) * mm});
            skSolve(sketch);
        }
        {
            var Q0;
            Q0=qCreatedBy(id+"F14.planeOp",FACE);
            var sketch = newSketch(context, id + "F16", { "sketchPlane" : qUnion([Q0])});
            skPoint(sketch, "E264.0", {"position": v(-8.45, -21) * mm});
            skPoint(sketch, "E265.0", {"position": v(-3.43, -20.16) * mm});
            skLineSegment(sketch, "E266", {"start": v(-8.45, -21) * mm, "end": v(-3.43, -20.16) * mm});
            skSolve(sketch);
        }
        {
            var Q0;
            Q0=sQuery(id+"F13.wireOp",VERTEX,"E250.0.start");
            var Q1;
            Q1=sQuery(id+"F11.wireOp",VERTEX,"E240.0.start");
            var Q2;
            Q2=sQuery(id+"F13.wireOp",VERTEX,"E251.0.end");
            cPlane(context, id + "F17", {"entities" : qUnion([Q0, Q1, Q2]), "cplaneType" : CPlaneType.THREE_POINT, "offset" : 25 * mm, "width" : 150 * mm, "height" : 150 * mm});
        }
        {
            var Q0;
            Q0=qCreatedBy(id+"F17.planeOp",FACE);
            var sketch = newSketch(context, id + "F18", { "sketchPlane" : qUnion([Q0])});
            skPoint(sketch, "E267.0", {"position": v(-13.42, 15.53) * mm});
            skPoint(sketch, "E268.0", {"position": v(-8.3, 16.05) * mm});
            skLineSegment(sketch, "E269", {"start": v(-13.42, 15.53) * mm, "end": v(-8.3, 16.05) * mm});
            skSolve(sketch);
        }
        {
            var Q0;
            Q0=qCreatedBy(id+"F17.planeOp",FACE);
            var sketch = newSketch(context, id + "F19", { "sketchPlane" : qUnion([Q0])});
            skPoint(sketch, "E270.0", {"position": v(-8.3, -16.05) * mm});
            skPoint(sketch, "E271.0", {"position": v(-13.42, -15.53) * mm});
            skLineSegment(sketch, "E272", {"start": v(-8.3, -16.05) * mm, "end": v(-13.42, -15.53) * mm});
            skSolve(sketch);
        }
        {
            var Q0;
            Q0=sQuery(id+"F13.wireOp",VERTEX,"E247.0.end");
            var Q1;
            Q1=sQuery(id+"F11.wireOp",VERTEX,"E242.0.start");
            var Q2;
            Q2=sQuery(id+"F13.wireOp",VERTEX,"E256.0.start");
            cPlane(context, id + "F20", {"entities" : qUnion([Q0, Q1, Q2]), "cplaneType" : CPlaneType.THREE_POINT, "offset" : 25 * mm, "width" : 150 * mm, "height" : 150 * mm});
        }
        {
            var Q0;
            Q0=qCreatedBy(id+"F20.planeOp",FACE);
            var sketch = newSketch(context, id + "F21", { "sketchPlane" : qUnion([Q0])});
            skPoint(sketch, "E273.0", {"position": v(-8.45, 21) * mm});
            skPoint(sketch, "E274.0", {"position": v(-3.43, 20.16) * mm});
            skLineSegment(sketch, "E275", {"start": v(-8.45, 21) * mm, "end": v(-3.43, 20.16) * mm});
            skSolve(sketch);
        }
        {
            var Q0;
            Q0=qCreatedBy(id+"F20.planeOp",FACE);
            var sketch = newSketch(context, id + "F22", { "sketchPlane" : qUnion([Q0])});
            skPoint(sketch, "E276.0", {"position": v(-8.45, -21) * mm});
            skPoint(sketch, "E277.0", {"position": v(-3.43, -20.16) * mm});
            skLineSegment(sketch, "E278", {"start": v(-8.45, -21) * mm, "end": v(-3.43, -20.16) * mm});
            skSolve(sketch);
        }
        {
            var Q0;
            Q0=sQuery(id+"F13.wireOp",VERTEX,"E246.0.start");
            var Q1;
            Q1=sQuery(id+"F11.wireOp",VERTEX,"E243.0.start");
            var Q2;
            Q2=sQuery(id+"F13.wireOp",VERTEX,"E259.0.start");
            cPlane(context, id + "F23", {"entities" : qUnion([Q0, Q1, Q2]), "cplaneType" : CPlaneType.THREE_POINT, "offset" : 25 * mm, "width" : 150 * mm, "height" : 150 * mm});
        }
        {
            var Q0;
            Q0=qCreatedBy(id+"F23.planeOp",FACE);
            var sketch = newSketch(context, id + "F24", { "sketchPlane" : qUnion([Q0])});
            skPoint(sketch, "E279.0", {"position": v(-13.42, -15.53) * mm});
            skPoint(sketch, "E280.0", {"position": v(-8.3, -16.05) * mm});
            skPoint(sketch, "E281.0", {"position": v(-13.42, 15.53) * mm});
            skPoint(sketch, "E282.0", {"position": v(-8.3, 16.05) * mm});
            skLineSegment(sketch, "E283", {"start": v(-13.42, 15.53) * mm, "end": v(-8.3, 16.05) * mm});
            skSolve(sketch);
        }
        {
            var Q0;
            Q0=qCreatedBy(id+"F23.planeOp",FACE);
            var sketch = newSketch(context, id + "F25", { "sketchPlane" : qUnion([Q0])});
            skPoint(sketch, "E284.0", {"position": v(-13.42, -15.53) * mm});
            skPoint(sketch, "E285.0", {"position": v(-8.3, -16.05) * mm});
            skLineSegment(sketch, "E286", {"start": v(-13.42, -15.53) * mm, "end": v(-8.3, -16.05) * mm});
            skSolve(sketch);
        }
        {
            var Q1;
            Q1=makeQuery(id+"F11.imprint","IMPRINT",FACE,{"disambiguationData":[TD([[makeQuery(id+"F11.imprint","IMPRINT",EDGE,{"derivedFrom":sQuery(id+"F11.wireOp",EDGE,"E236.0")}),-1.0]])]});
            var Q2;
            Q2=makeQuery(id+"F13.imprint","IMPRINT",FACE,{"disambiguationData":[TD([[makeQuery(id+"F13.imprint","IMPRINT",EDGE,{"derivedFrom":sQuery(id+"F13.wireOp",EDGE,"E246.0")}),1.0]])]});
            var Q3;
            Q3=sQuery(id+"F15.wireOp",EDGE,"E263");
            var Q4;
            Q4=sQuery(id+"F18.wireOp",EDGE,"E269");
            var Q5;
            Q5=sQuery(id+"F19.wireOp",EDGE,"E272");
            var Q6;
            Q6=sQuery(id+"F16.wireOp",EDGE,"E266");
            var Q7;
            Q7=sQuery(id+"F22.wireOp",EDGE,"E278");
            var Q8;
            Q8=sQuery(id+"F25.wireOp",EDGE,"E286");
            var Q9;
            Q9=sQuery(id+"F24.wireOp",EDGE,"E283");
            var Q10;
            Q10=sQuery(id+"F21.wireOp",EDGE,"E275");
            loft(context, id + "F26", {"operationType" : NewBodyOperationType.ADD, "addGuides" : true, "sheetProfilesArray" : [{ "sheetProfileEntities" : qUnion([Q1]) }, { "sheetProfileEntities" : qUnion([Q2]) }], "guidesArray" : [{ "guideEntities" : qUnion([Q3]), "guideDerivativeType" : LoftGuideDerivativeType.DEFAULT, "guideDerivativeMagnitude" : 1 }, { "guideEntities" : qUnion([Q4]), "guideDerivativeType" : LoftGuideDerivativeType.DEFAULT, "guideDerivativeMagnitude" : 1 }, { "guideEntities" : qUnion([Q5]), "guideDerivativeType" : LoftGuideDerivativeType.DEFAULT, "guideDerivativeMagnitude" : 1 }, { "guideEntities" : qUnion([Q6]), "guideDerivativeType" : LoftGuideDerivativeType.DEFAULT, "guideDerivativeMagnitude" : 1 }, { "guideEntities" : qUnion([Q7]), "guideDerivativeType" : LoftGuideDerivativeType.DEFAULT, "guideDerivativeMagnitude" : 1 }, { "guideEntities" : qUnion([Q8]), "guideDerivativeType" : LoftGuideDerivativeType.DEFAULT, "guideDerivativeMagnitude" : 1 }, { "guideEntities" : qUnion([Q9]), "guideDerivativeType" : LoftGuideDerivativeType.DEFAULT, "guideDerivativeMagnitude" : 1 }, { "guideEntities" : qUnion([Q10]), "guideDerivativeType" : LoftGuideDerivativeType.DEFAULT, "guideDerivativeMagnitude" : 1 }]});
        }
        {
            var Q0;
            Q0=makeQuery(id+"F13.imprint","IMPRINT",FACE,{"disambiguationData":[TD([[makeQuery(id+"F13.imprint","IMPRINT",EDGE,{"derivedFrom":sQuery(id+"F13.wireOp",EDGE,"E246.0")}),1.0]])]});
            var sketch = newSketch(context, id + "F27", { "sketchPlane" : qUnion([Q0])});
            skFitSpline(sketch, "E287.0", {"points": [v(-21.22, 15.53) * mm, v(-19.57, 17.8) * mm, v(-17.9, 19.35) * mm, v(-15.77, 21) * mm]});
            skLineSegment(sketch, "E288.0", {"start": v(-21.22, 15.53) * mm, "end": v(-21.22, -15.53) * mm});
            skLineSegment(sketch, "E289.0", {"start": v(-15.77, -21) * mm, "end": v(0, -21) * mm});
            skFitSpline(sketch, "E290.0", {"points": [v(-21.22, -15.53) * mm, v(-19.57, -17.8) * mm, v(-17.9, -19.35) * mm, v(-15.77, -21) * mm]});
            skFitSpline(sketch, "E291.0", {"points": [v(-21.22, -15.53) * mm, v(-19.57, -17.8) * mm, v(-17.9, -19.35) * mm, v(-15.77, -21) * mm]});
            skFitSpline(sketch, "E292.0", {"points": [v(-21.22, -15.53) * mm, v(-19.57, -17.8) * mm, v(-17.9, -19.35) * mm, v(-15.77, -21) * mm]});
            skLineSegment(sketch, "E293.0", {"start": v(-15.77, 21) * mm, "end": v(0, 21) * mm});
            skLineSegment(sketch, "E294.0", {"start": v(15.77, 21) * mm, "end": v(0, 21) * mm});
            skFitSpline(sketch, "E295.0", {"points": [v(21.22, 15.53) * mm, v(19.57, 17.8) * mm, v(17.9, 19.35) * mm, v(15.77, 21) * mm]});
            skFitSpline(sketch, "E296.0", {"points": [v(21.22, 15.53) * mm, v(19.57, 17.8) * mm, v(17.9, 19.35) * mm, v(15.77, 21) * mm]});
            skLineSegment(sketch, "E297.0", {"start": v(21.22, -15.53) * mm, "end": v(21.22, 15.53) * mm});
            skLineSegment(sketch, "E298.0", {"start": v(15.77, -21) * mm, "end": v(0, -21) * mm});
            skFitSpline(sketch, "E299.0", {"points": [v(21.22, -15.53) * mm, v(19.57, -17.8) * mm, v(17.9, -19.35) * mm, v(15.77, -21) * mm]});
            skFitSpline(sketch, "E300.0", {"points": [v(21.22, -15.53) * mm, v(19.57, -17.8) * mm, v(17.9, -19.35) * mm, v(15.77, -21) * mm]});
            skFitSpline(sketch, "E301.0", {"points": [v(21.22, -15.53) * mm, v(19.57, -17.8) * mm, v(17.9, -19.35) * mm, v(15.77, -21) * mm]});
            skSolve(sketch);
        }
        {
            var Q0;
            Q0 = qSketchRegion(id + "F27", true);
            extrude(context, id + "F28", {"entities" : qUnion([Q0]), "oppositeDirection" : true, "depth" : 34.1 * mm, "offsetDistance" : 25 * mm});
        }
        {
            var Q0;
            Q0=makeQuery(id+"F28.opExtrude","CAP_EDGE",EDGE,{"disambiguationData":[OSD([sQuery(id+"F27.wireOp",EDGE,"E293.0"),sQuery(id+"F27.wireOp",EDGE,"E294.0")])],"isStart":false});
            var Q1;
            Q1=makeQuery(id+"F28.opExtrude","CAP_EDGE",EDGE,{"disambiguationData":[OSD([sQuery(id+"F27.wireOp",EDGE,"E295.0"),sQuery(id+"F27.wireOp",EDGE,"E296.0")])],"isStart":false});
            var Q2;
            Q2=makeQuery(id+"F28.opExtrude","CAP_EDGE",EDGE,{"disambiguationData":[OSD([sQuery(id+"F27.wireOp",EDGE,"E297.0")])],"isStart":false});
            var Q3;
            Q3=makeQuery(id+"F28.opExtrude","CAP_EDGE",EDGE,{"disambiguationData":[OSD([sQuery(id+"F27.wireOp",EDGE,"E287.0")])],"isStart":false});
            var Q4;
            Q4=makeQuery(id+"F28.opExtrude","CAP_EDGE",EDGE,{"disambiguationData":[OSD([sQuery(id+"F27.wireOp",EDGE,"E288.0")])],"isStart":false});
            var Q5;
            Q5=makeQuery(id+"F28.opExtrude","CAP_EDGE",EDGE,{"disambiguationData":[OSD([sQuery(id+"F27.wireOp",EDGE,"E290.0"),sQuery(id+"F27.wireOp",EDGE,"E291.0"),sQuery(id+"F27.wireOp",EDGE,"E292.0")])],"isStart":false});
            var Q6;
            Q6=makeQuery(id+"F28.opExtrude","CAP_EDGE",EDGE,{"disambiguationData":[OSD([sQuery(id+"F27.wireOp",EDGE,"E289.0"),sQuery(id+"F27.wireOp",EDGE,"E298.0")])],"isStart":false});
            var Q7;
            Q7=makeQuery(id+"F28.opExtrude","CAP_EDGE",EDGE,{"disambiguationData":[OSD([sQuery(id+"F27.wireOp",EDGE,"E299.0"),sQuery(id+"F27.wireOp",EDGE,"E300.0"),sQuery(id+"F27.wireOp",EDGE,"E301.0")])],"isStart":false});
            chamfer(context, id + "F29", {"entities" : qUnion([Q0, Q1, Q2, Q3, Q4, Q5, Q6, Q7]), "width" : 0.5 * mm, "tangentPropagation" : true});
        }
    });
